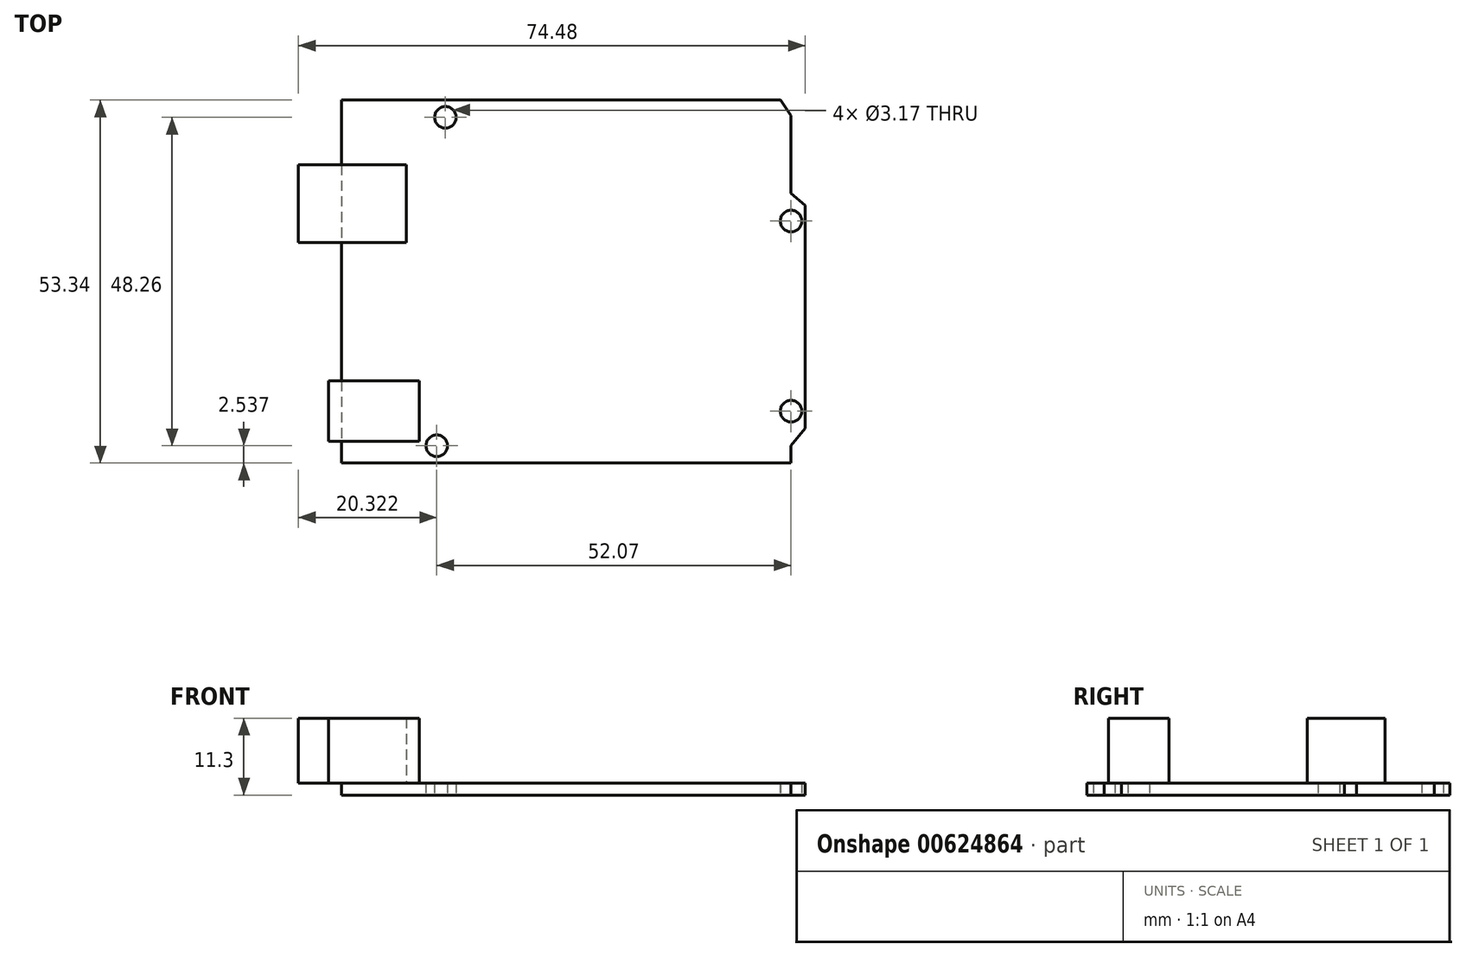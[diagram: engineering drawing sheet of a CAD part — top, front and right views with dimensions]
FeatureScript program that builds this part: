
annotation { "Feature Type Name" : "Feature", "Feature Type Description" : "" }
export const myFeature = defineFeature(function(context is Context, id is Id, definition is map)
    precondition{}
    {
        {
            var Q0;
            Q0=qCreatedBy(makeId("Top.planeOp"),FACE);
            var sketch = newSketch(context, id + "F0", { "sketchPlane" : qUnion([Q0])});
            skLineSegment(sketch, "E0", {"start": v(-32.5, 27) * mm, "end": v(-32.5, -26.34) * mm});
            skLineSegment(sketch, "E1", {"start": v(-32.5, 27) * mm, "end": v(32.02, 27) * mm});
            skLineSegment(sketch, "E2", {"start": v(32.02, 27) * mm, "end": v(33.54, 24.7) * mm});
            skLineSegment(sketch, "E3", {"start": v(-32.5, -26.34) * mm, "end": v(33.54, -26.34) * mm});
            skLineSegment(sketch, "E4", {"start": v(33.54, 24.7) * mm, "end": v(33.54, 13.28) * mm});
            skLineSegment(sketch, "E5", {"start": v(33.54, 13.28) * mm, "end": v(35.63, 11.5) * mm});
            skLineSegment(sketch, "E6", {"start": v(35.63, 11.5) * mm, "end": v(35.63, -21.26) * mm});
            skLineSegment(sketch, "E7", {"start": v(33.54, -26.34) * mm, "end": v(33.54, -23.8) * mm});
            skLineSegment(sketch, "E8", {"start": v(33.54, -23.8) * mm, "end": v(35.63, -21.26) * mm});
            skCircle(sketch, "E9", {"center": v(33.54, -18.72) * mm, "radius": 1.59 * mm});
            skLineSegment(sketch, "E10", {"start": v(33.54, -18.72) * mm, "end": v(33.54, -17.14) * mm});
            skCircle(sketch, "E11", {"center": v(33.54, 9.22) * mm, "radius": 1.59 * mm});
            skCircle(sketch, "E12", {"center": v(-18.53, -23.8) * mm, "radius": 1.59 * mm});
            skPoint(sketch, "E13.start.orphan", {"position": v(-18.53, -26.34) * mm});
            skLineSegment(sketch, "E14", {"start": v(-17.26, -26.34) * mm, "end": v(-17.26, -22.85) * mm});
            skCircle(sketch, "E15", {"center": v(-17.26, 24.46) * mm, "radius": 1.59 * mm});
            skSolve(sketch);
        }
        {
            var Q0;
            Q0=qSketchRegion(id+"F0",true);
            extrude(context, id + "F1", {"entities" : qUnion([Q0]), "depth" : 1.78 * mm, "offsetDistance" : 25.4 * mm});
        }
        {
            var Q0;
            Q0=makeQuery(id+"F1.opExtrude","CAP_FACE",FACE,{"disambiguationData":[OSD([sQuery(id+"F0.wireOp",EDGE,"E0"),sQuery(id+"F0.wireOp",EDGE,"E1"),sQuery(id+"F0.wireOp",EDGE,"E2"),sQuery(id+"F0.wireOp",EDGE,"E3"),sQuery(id+"F0.wireOp",EDGE,"E4"),sQuery(id+"F0.wireOp",EDGE,"E5"),sQuery(id+"F0.wireOp",EDGE,"E6"),sQuery(id+"F0.wireOp",EDGE,"E8"),sQuery(id+"F0.wireOp",EDGE,"E7"),sQuery(id+"F0.wireOp",EDGE,"E9"),sQuery(id+"F0.wireOp",EDGE,"E11"),sQuery(id+"F0.wireOp",EDGE,"E12"),sQuery(id+"F0.wireOp",EDGE,"E15")])],"isStart":false});
            var sketch = newSketch(context, id + "F2", { "sketchPlane" : qUnion([Q0])});
            skPoint(sketch, "E16.orphan", {"position": v(-39.38, -26.36) * mm});
            skPoint(sketch, "E17.end.orphan", {"position": v(-45.76, -26.36) * mm});
            skPoint(sketch, "E18.start.orphan", {"position": v(-33, -26.36) * mm});
            skLineSegment(sketch, "E19", {"start": v(-23.15, 6.04) * mm, "end": v(-23.15, 6.04) * mm});
            skPoint(sketch, "E20.start.orphan", {"position": v(-32.68, 6.04) * mm});
            skLineSegment(sketch, "E21", {"start": v(-32.5, 6.04) * mm, "end": v(-22.97, 6.04) * mm});
            skLineSegment(sketch, "E22", {"start": v(-22.97, 6.04) * mm, "end": v(-22.97, 17.47) * mm});
            skPoint(sketch, "E23.end.orphan", {"position": v(-35, 6.04) * mm});
            skLineSegment(sketch, "E24", {"start": v(-22.97, 17.47) * mm, "end": v(-38.85, 17.47) * mm});
            skLineSegment(sketch, "E25", {"start": v(-38.85, 17.47) * mm, "end": v(-38.85, 6.04) * mm});
            skLineSegment(sketch, "E26", {"start": v(-32.5, 6.04) * mm, "end": v(-38.85, 6.04) * mm});
            skPoint(sketch, "E27.end.orphan", {"position": v(-21.57, -17.47) * mm});
            skPoint(sketch, "E28.start.orphan", {"position": v(-21.57, -23.17) * mm});
            skLineSegment(sketch, "E29", {"start": v(-32.5, -23.17) * mm, "end": v(-21.07, -23.17) * mm});
            skPoint(sketch, "E30.end.orphan", {"position": v(-34.9, -17.47) * mm});
            skPoint(sketch, "E31.end.orphan", {"position": v(-34.9, -26.36) * mm});
            skPoint(sketch, "E32.end.orphan", {"position": v(-21.57, -26.35) * mm});
            skLineSegment(sketch, "E33", {"start": v(-34.4, -23.17) * mm, "end": v(-32.5, -23.17) * mm});
            skLineSegment(sketch, "E34", {"start": v(-34.4, -23.17) * mm, "end": v(-34.4, -14.28) * mm});
            skLineSegment(sketch, "E35", {"start": v(-34.4, -14.28) * mm, "end": v(-21.07, -14.28) * mm});
            skLineSegment(sketch, "E36", {"start": v(-21.07, -14.28) * mm, "end": v(-21.07, -23.17) * mm});
            skPoint(sketch, "E37.end.orphan", {"position": v(-14.78, 6.04) * mm});
            skPoint(sketch, "E37.start.orphan", {"position": v(-14.78, -26.36) * mm});
            skPoint(sketch, "E38.end.orphan", {"position": v(-19.07, -23.17) * mm});
            skPoint(sketch, "E38.start.orphan", {"position": v(-19.07, -26.35) * mm});
            skLineSegment(sketch, "E39", {"start": v(-32.5, 27) * mm, "end": v(-32.5, 17.47) * mm});
            skSolve(sketch);
        }
        {
            var Q0;
            Q0=qSketchRegion(id+"F2",true);
            extrude(context, id + "F3", {"entities" : qUnion([Q0]), "depth" : 9.52 * mm, "offsetDistance" : 25.4 * mm});
        }
    });
